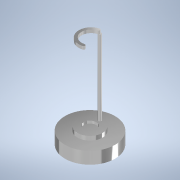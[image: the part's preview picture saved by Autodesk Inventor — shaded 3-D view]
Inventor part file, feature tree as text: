
AUTODESK INVENTOR PART (.ipt)
format: ipt  version: 2021 (Build 250183000, 183)  size: 152,576 bytes
history: native  units: mm (DEFAULTED — no unit token found)
features: extrude x2, sketch x2
ambient origin geometry x8: Origin, YZ Plane, XZ Plane, XY Plane, X Axis, Y Axis, Z Axis, Center Point
bodies: Solid1 (feature_tree)
feature tree (4):
  extrude  "Extrusion4"  Depth=19.3mm TaperAngle=0.0deg
  extrude  "Extrusion5"  Depth=6.5mm TaperAngle=0.0deg
  sketch  "Sketch4"  dims[d0=80.0mm d1=19.3mm d2=0.0mm]
  sketch  "Sketch5"  dims[d3=40.0mm d4=6.5mm d5=0.0mm d6=20.0mm d7=4.0mm d8=0.0mm d9=15.75mm d10=5.0mm d11=120.0mm d12=0.0mm d13=5.0mm d14=0.0mm]
